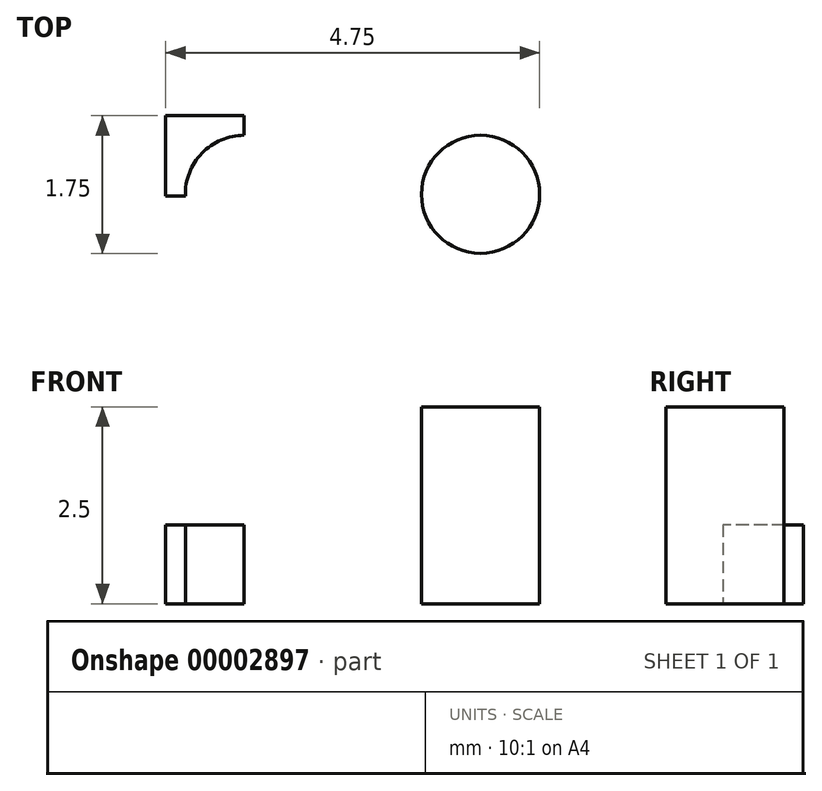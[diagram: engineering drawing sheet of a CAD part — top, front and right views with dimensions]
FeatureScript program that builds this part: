
annotation { "Feature Type Name" : "Feature", "Feature Type Description" : "" }
export const myFeature = defineFeature(function(context is Context, id is Id, definition is map)
    precondition{}
    {
        {
            var Q0;
            Q0=qCreatedBy(makeId("Top.planeOp"),FACE);
            var sketch = newSketch(context, id + "F0", { "sketchPlane" : qUnion([Q0])});
            skLineSegment(sketch, "E0.bottom", {"start": v(0.74, 3.07) * mm, "end": v(5.74, 3.07) * mm});
            skLineSegment(sketch, "E0.top", {"start": v(0.74, 1.07) * mm, "end": v(5.74, 1.07) * mm});
            skLineSegment(sketch, "E0.left", {"start": v(0.74, 3.07) * mm, "end": v(0.74, 1.07) * mm});
            skLineSegment(sketch, "E0.right", {"start": v(5.74, 3.07) * mm, "end": v(5.74, 1.07) * mm});
            skCircle(sketch, "E1", {"center": v(1.74, 2.07) * mm, "radius": 0.75 * mm});
            skCircle(sketch, "E2", {"center": v(4.74, 2.07) * mm, "radius": 0.75 * mm});
            skLineSegment(sketch, "E3", {"start": v(1.74, 2.07) * mm, "end": v(4.74, 2.07) * mm});
            skLineSegment(sketch, "E4", {"start": v(1, 2.05) * mm, "end": v(0.74, 2.05) * mm});
            skLineSegment(sketch, "E5", {"start": v(1.74, 2.82) * mm, "end": v(1.74, 3.07) * mm});
            skSolve(sketch);
        }
        {
            var Q0;
            {var subQ0=sQuery(id+"F0.wireOp",EDGE,"E3");Q0=makeQuery(id+"F0.imprint","IMPRINT",FACE,{"disambiguationData":[TD([[makeQuery(id+"F0.imprint","IMPRINT",EDGE,{"disambiguationData":[TD([[makeQuery(id+"F0.imprint","IMPRINT",VERTEX,{"derivedFrom":sQuery(id+"F0.wireOp",VERTEX,"E3.start")}),-1.0]])],"derivedFrom":subQ0}),1.0]])]});}
            var Q1;
            {var subQ1=sQuery(id+"F0.wireOp",EDGE,"E2");Q1=makeQuery(id+"F0.imprint","IMPRINT",FACE,{"disambiguationData":[TD([[makeQuery(id+"F0.imprint","IMPRINT",EDGE,{"derivedFrom":subQ1}),1.0]])]});}
            extrude(context, id + "F1", {"entities" : qUnion([Q0, Q1]), "depth" : 2.5 * mm});
        }
        {
            var Q0;
            {var subQ1=sQuery(id+"F0.wireOp",EDGE,"E4");Q0=makeQuery(id+"F0.imprint","IMPRINT",FACE,{"disambiguationData":[TD([[makeQuery(id+"F0.imprint","IMPRINT",EDGE,{"derivedFrom":subQ1}),-1.0]])]});}
            extrude(context, id + "F2", {"entities" : qUnion([Q0]), "depth" : 1 * mm});
        }
    });
